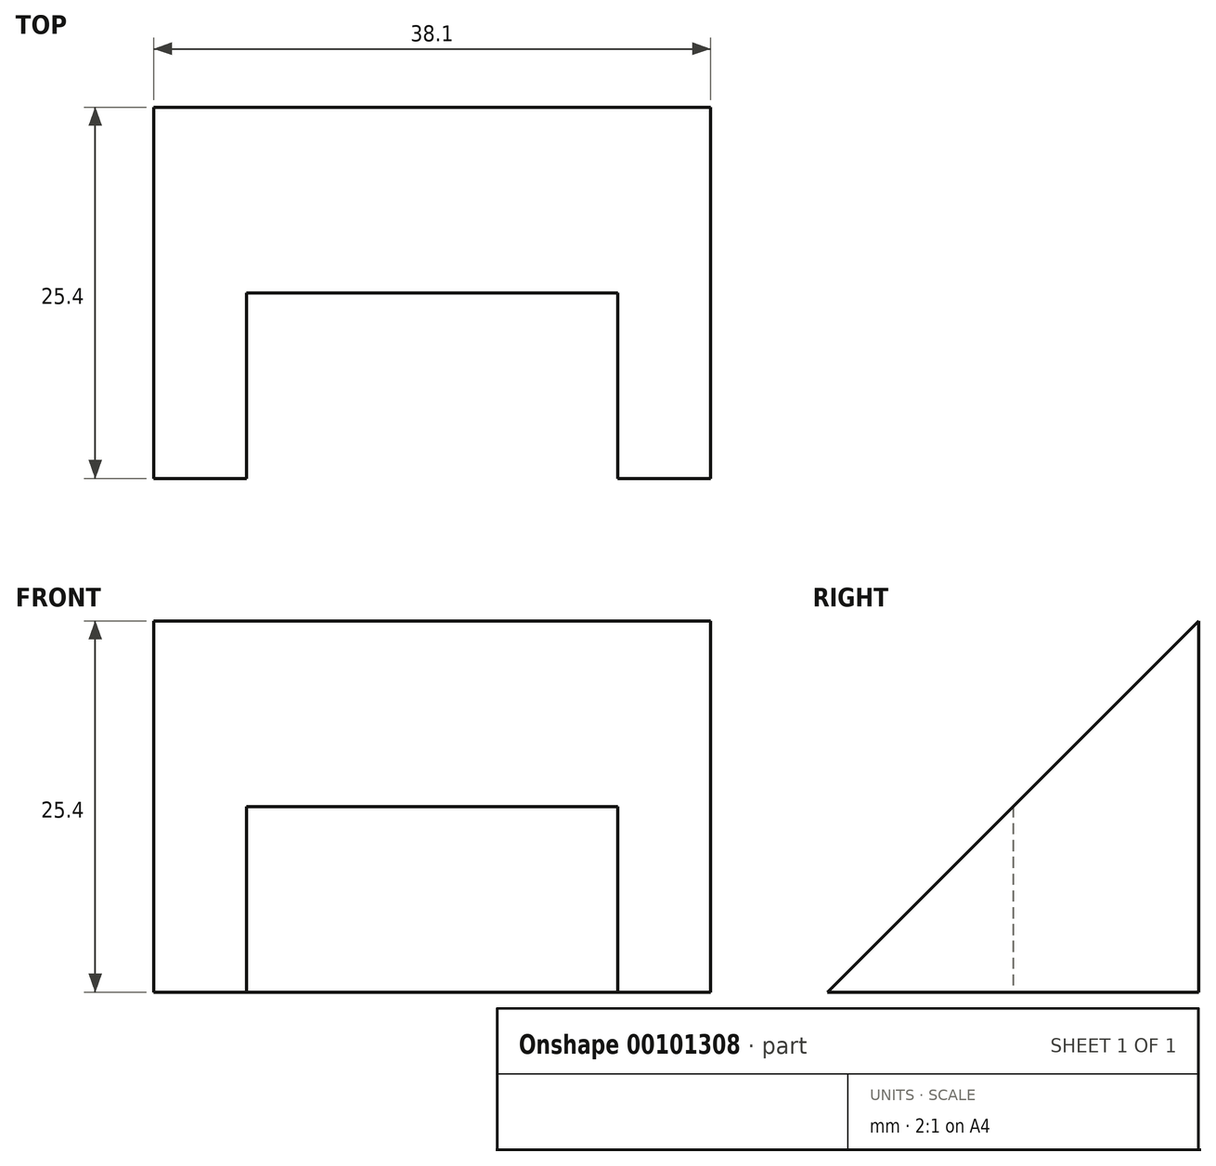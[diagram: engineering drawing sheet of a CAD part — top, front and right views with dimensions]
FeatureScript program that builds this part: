
annotation { "Feature Type Name" : "Feature", "Feature Type Description" : "" }
export const myFeature = defineFeature(function(context is Context, id is Id, definition is map)
    precondition{}
    {
        {
            var Q0;
            Q0=qCreatedBy(makeId("Right.planeOp"),FACE);
            var sketch = newSketch(context, id + "F0", { "sketchPlane" : qUnion([Q0])});
            skLineSegment(sketch, "E0", {"start": v(0, 0) * mm, "end": v(25.4, 0) * mm});
            skLineSegment(sketch, "E1", {"start": v(25.4, 0) * mm, "end": v(25.4, 25.4) * mm});
            skLineSegment(sketch, "E2", {"start": v(25.4, 25.4) * mm, "end": v(0, 0) * mm});
            skSolve(sketch);
        }
        {
            var Q0;
            Q0 = qSketchRegion(id + "F0", true);
            extrude(context, id + "F1", {"entities" : qUnion([Q0]), "oppositeDirection" : true, "depth" : 38.1 * mm});
        }
        {
            var Q0;
            Q0=qCreatedBy(makeId("Top.planeOp"),FACE);
            var sketch = newSketch(context, id + "F2", { "sketchPlane" : qUnion([Q0])});
            skLineSegment(sketch, "E3", {"start": v(-31.75, 0) * mm, "end": v(-31.75, 12.7) * mm});
            skLineSegment(sketch, "E4", {"start": v(-31.75, 12.7) * mm, "end": v(-6.35, 12.7) * mm});
            skLineSegment(sketch, "E5", {"start": v(-6.35, 12.7) * mm, "end": v(-6.35, 0) * mm});
            skLineSegment(sketch, "E6", {"start": v(-6.35, 0) * mm, "end": v(-31.75, 0) * mm});
            skSolve(sketch);
        }
        {
            var Q0;
            Q0 = qSketchRegion(id + "F2", true);
            extrude(context, id + "F3", {"entities" : qUnion([Q0]), "operationType" : NewBodyOperationType.REMOVE, "endBound" : BoundingType.THROUGH_ALL, "depth" : 25.4 * mm});
        }
    });
